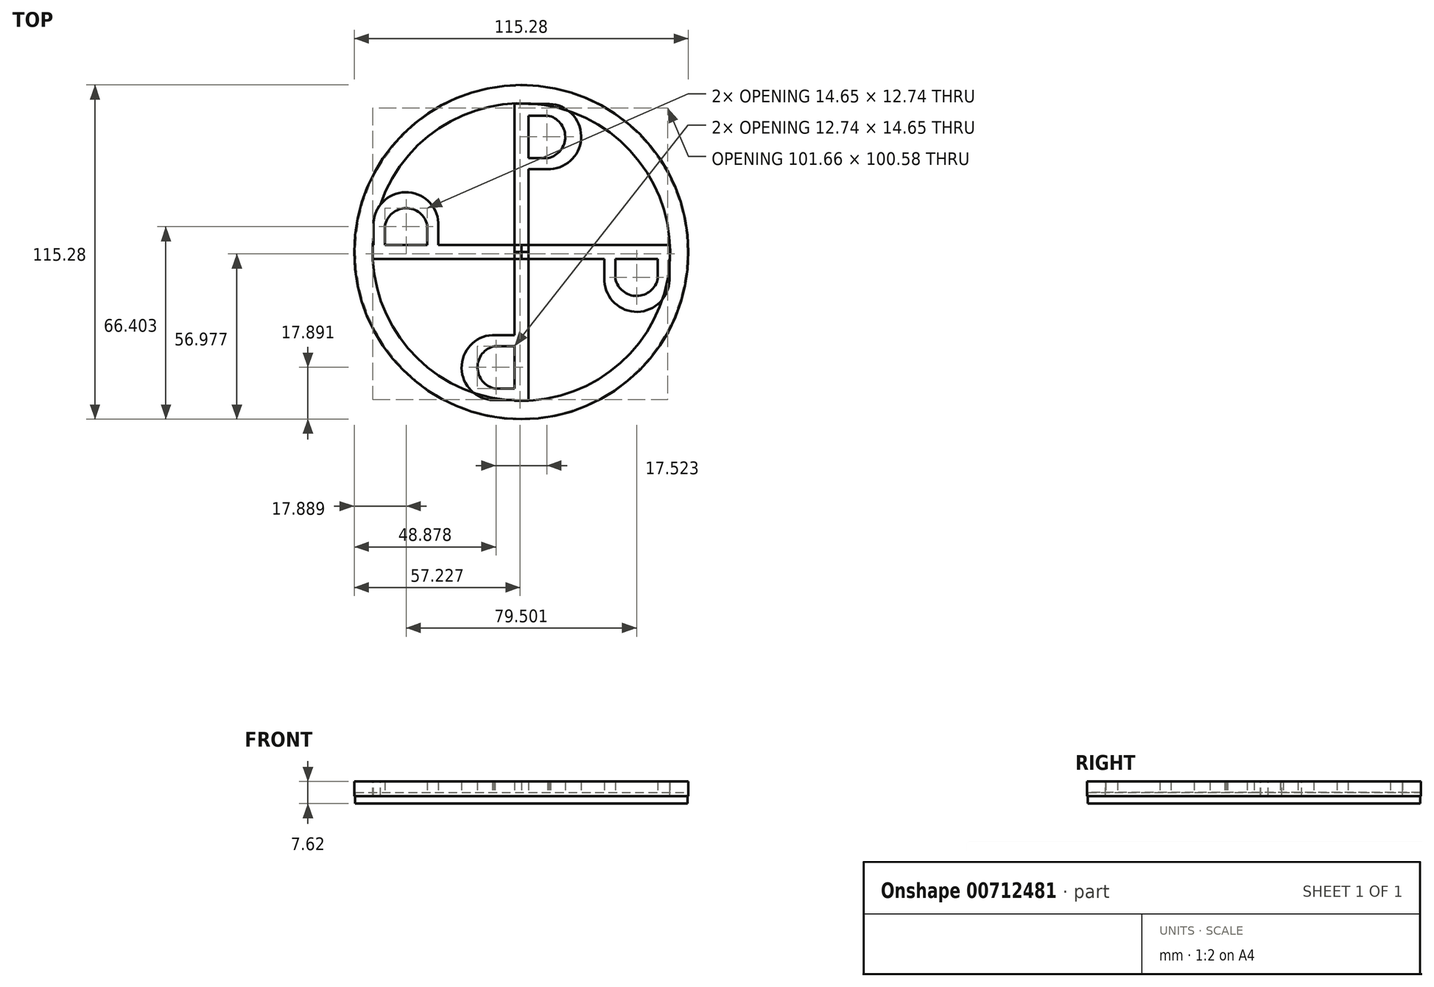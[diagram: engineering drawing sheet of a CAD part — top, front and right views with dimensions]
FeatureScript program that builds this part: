
annotation { "Feature Type Name" : "Feature", "Feature Type Description" : "" }
export const myFeature = defineFeature(function(context is Context, id is Id, definition is map)
    precondition{}
    {
        {
            var Q0;
            Q0=qCreatedBy(makeId("Top.planeOp"),FACE);
            var sketch = newSketch(context, id + "F0", { "sketchPlane" : qUnion([Q0])});
            skLineSegment(sketch, "E0", {"start": v(-10.04, 28.15) * mm, "end": v(-10.04, -23.09) * mm});
            skLineSegment(sketch, "E1", {"start": v(-10.04, -23.09) * mm, "end": v(-5.26, -23.09) * mm});
            skLineSegment(sketch, "E2", {"start": v(-5.26, -23.09) * mm, "end": v(-5.26, 28.15) * mm});
            skLineSegment(sketch, "E3", {"start": v(-5.26, 28.15) * mm, "end": v(-10.04, 28.15) * mm});
            skArc(sketch, "E4", {"start": v(2.4, 5.54) * mm, "mid": v(12.97, 16.95) * mm, "end": v(1.98, 27.97) * mm});
            skLineSegment(sketch, "E5", {"start": v(1.98, 27.97) * mm, "end": v(-5.26, 27.97) * mm});
            skLineSegment(sketch, "E6", {"start": v(2.4, 5.54) * mm, "end": v(-5.26, 5.54) * mm});
            skArc(sketch, "E7", {"start": v(1.58, 9.34) * mm, "mid": v(7.48, 16.73) * mm, "end": v(1.4, 23.98) * mm});
            skLineSegment(sketch, "E8", {"start": v(1.4, 23.98) * mm, "end": v(-5.26, 23.98) * mm});
            skLineSegment(sketch, "E9", {"start": v(1.58, 9.34) * mm, "end": v(-5.26, 9.34) * mm});
            skSolve(sketch);
        }
        {
            var Q0;
            Q0=qSketchRegion(id+"F0",true);
            extrude(context, id + "F1", {"entities" : qUnion([Q0]), "depth" : 5.08 * mm, "offsetDistance" : 25.4 * mm});
        }
        {
            var Q0;
            Q0=makeQuery(id+"F1.opExtrude","SWEPT_FACE",FACE,{"disambiguationData":[OSD([sQuery(id+"F0.wireOp",EDGE,"E1")])]});
            var sketch = newSketch(context, id + "F2", { "sketchPlane" : qUnion([Q0])});
            skLineSegment(sketch, "E10", {"start": v(-7.65, 5.08) * mm, "end": v(-7.65, 0) * mm});
            skSolve(sketch);
        }
        {
            var Q0;
            Q0=makeQuery(id+"F1.opExtrude","SWEPT_BODY",BODY,{"disambiguationData":[OSD([sQuery(id+"F0.wireOp",EDGE,"E0"),sQuery(id+"F0.wireOp",EDGE,"E1"),sQuery(id+"F0.wireOp",EDGE,"E2"),sQuery(id+"F0.wireOp",EDGE,"E3"),sQuery(id+"F0.wireOp",EDGE,"E4"),sQuery(id+"F0.wireOp",EDGE,"E5"),sQuery(id+"F0.wireOp",EDGE,"E6"),sQuery(id+"F0.wireOp",EDGE,"E7"),sQuery(id+"F0.wireOp",EDGE,"E8"),sQuery(id+"F0.wireOp",EDGE,"E9")])]});
            var Q1;
            Q1=sQuery(id+"F2.wireOp",EDGE,"E10");
            circularPattern(context, id + "F3", {"entities" : qUnion([Q0]), "axis" : qUnion([Q1]), "angle" : 360 * degree, "instanceCount" : 4, "equalSpace" : true});
        }
        {
            var Q0;
            Q0=makeQuery(id+"F3.opPattern","COPY",FACE,{"derivedFrom":makeQuery(id+"F1.opExtrude","CAP_FACE",FACE,{"disambiguationData":[OSD([sQuery(id+"F0.wireOp",EDGE,"E0"),sQuery(id+"F0.wireOp",EDGE,"E1"),sQuery(id+"F0.wireOp",EDGE,"E2"),sQuery(id+"F0.wireOp",EDGE,"E3"),sQuery(id+"F0.wireOp",EDGE,"E4"),sQuery(id+"F0.wireOp",EDGE,"E5"),sQuery(id+"F0.wireOp",EDGE,"E6"),sQuery(id+"F0.wireOp",EDGE,"E7"),sQuery(id+"F0.wireOp",EDGE,"E8"),sQuery(id+"F0.wireOp",EDGE,"E9")])],"isStart":false}),"instanceName":"3"});
            var sketch = newSketch(context, id + "F4", { "sketchPlane" : qUnion([Q0])});
            skCircle(sketch, "E11", {"center": v(-7.65, -23.09) * mm, "radius": 51.3 * mm});
            skCircle(sketch, "E12.0", {"center": v(-7.65, -23.09) * mm, "radius": 57.64 * mm});
            skSolve(sketch);
        }
        {
            var Q0;
            Q0=makeQuery(id+"F4.imprint","IMPRINT",FACE,{"disambiguationData":[TD([[makeQuery(id+"F4.imprint","IMPRINT",EDGE,{"derivedFrom":sQuery(id+"F4.wireOp",EDGE,"E12.0")}),1.0]])]});
            extrude(context, id + "F5", {"entities" : qUnion([Q0]), "oppositeDirection" : true, "depth" : 5.08 * mm, "offsetDistance" : 25.4 * mm});
        }
        {
            var Q0;
            Q0=makeQuery(id+"F3.opPattern","COPY",FACE,{"derivedFrom":makeQuery(id+"F1.opExtrude","CAP_FACE",FACE,{"disambiguationData":[OSD([sQuery(id+"F0.wireOp",EDGE,"E0"),sQuery(id+"F0.wireOp",EDGE,"E1"),sQuery(id+"F0.wireOp",EDGE,"E2"),sQuery(id+"F0.wireOp",EDGE,"E3"),sQuery(id+"F0.wireOp",EDGE,"E4"),sQuery(id+"F0.wireOp",EDGE,"E5"),sQuery(id+"F0.wireOp",EDGE,"E6"),sQuery(id+"F0.wireOp",EDGE,"E7"),sQuery(id+"F0.wireOp",EDGE,"E8"),sQuery(id+"F0.wireOp",EDGE,"E9")])],"isStart":true}),"instanceName":"2"});
            var sketch = newSketch(context, id + "F6", { "sketchPlane" : qUnion([Q0])});
            skCircle(sketch, "E13", {"center": v(-7.65, 23.09) * mm, "radius": 57.34 * mm});
            skSolve(sketch);
        }
        {
            var Q0;
            Q0=qSketchRegion(id+"F6",true);
            extrude(context, id + "F7", {"entities" : qUnion([Q0]), "depth" : 2.54 * mm, "offsetDistance" : 25.4 * mm});
        }
        {
            var Q0;
            Q0=makeQuery(id+"F7.opExtrude","CAP_FACE",FACE,{"disambiguationData":[OSD([sQuery(id+"F6.wireOp",EDGE,"E13")])],"isStart":true});
            extrude(context, id + "F8", {"entities" : qUnion([Q0]), "depth" : 1.27 * mm, "offsetDistance" : 25.4 * mm});
        }
    });
